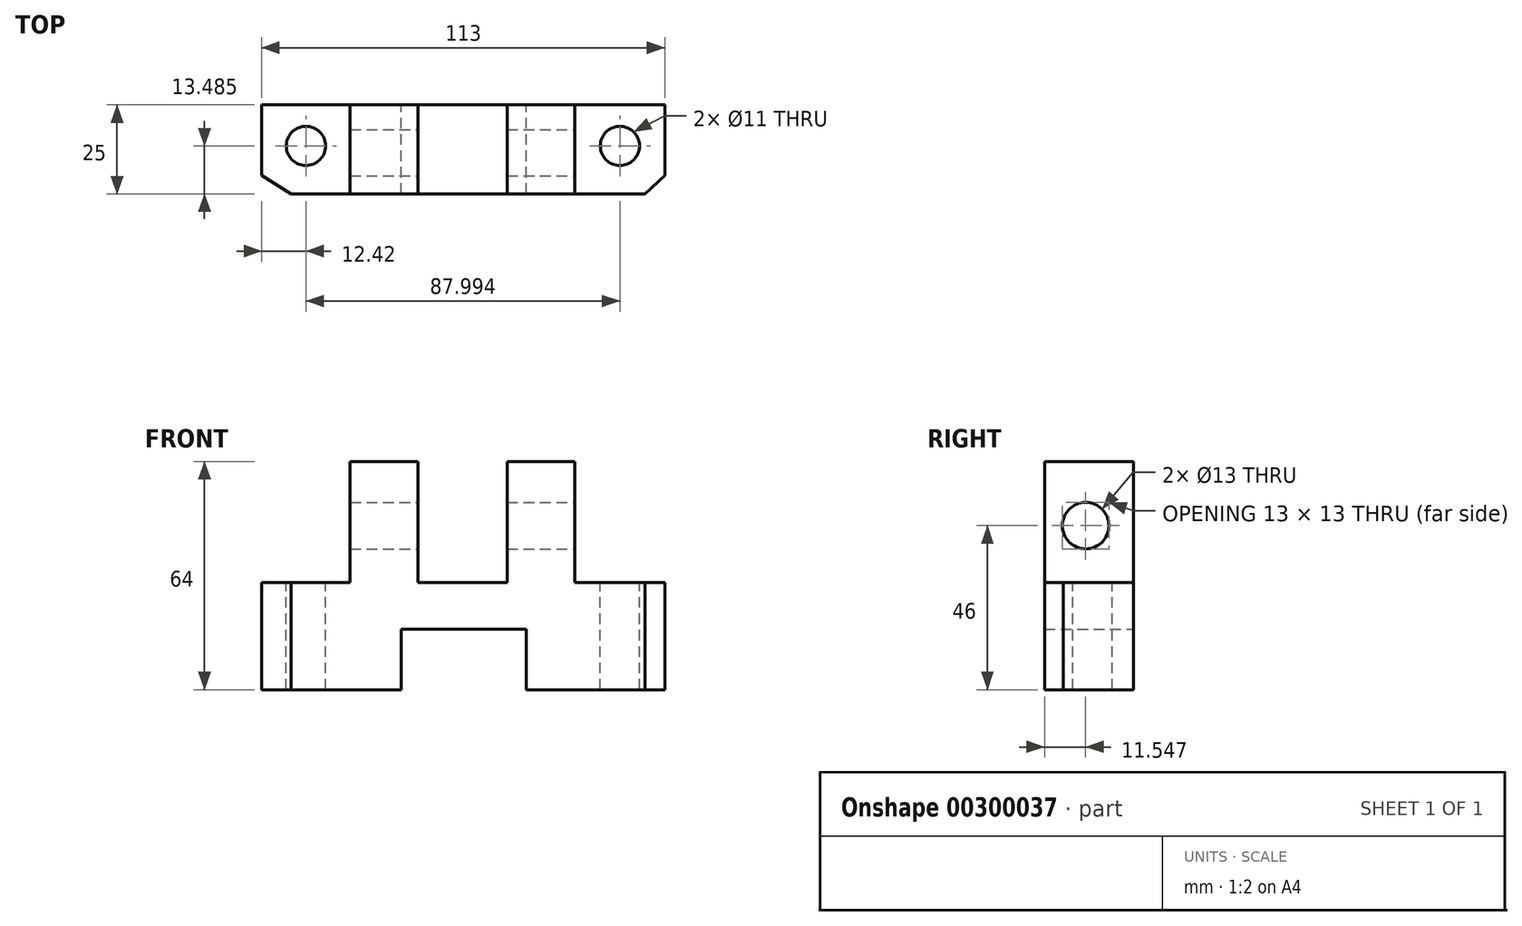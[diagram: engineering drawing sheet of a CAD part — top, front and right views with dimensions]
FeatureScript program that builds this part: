
annotation { "Feature Type Name" : "Feature", "Feature Type Description" : "" }
export const myFeature = defineFeature(function(context is Context, id is Id, definition is map)
    precondition{}
    {
        {
            var Q0;
            Q0=qCreatedBy(makeId("Front.planeOp"),FACE);
            var sketch = newSketch(context, id + "F0", { "sketchPlane" : qUnion([Q0])});
            skLineSegment(sketch, "E0", {"start": v(0, 0) * mm, "end": v(0, 30) * mm});
            skLineSegment(sketch, "E1", {"start": v(0, 30) * mm, "end": v(24.83, 30) * mm});
            skLineSegment(sketch, "E2", {"start": v(24.83, 30) * mm, "end": v(24.83, 64) * mm});
            skLineSegment(sketch, "E3", {"start": v(24.83, 64) * mm, "end": v(43.83, 64) * mm});
            skLineSegment(sketch, "E4", {"start": v(43.83, 64) * mm, "end": v(43.83, 30) * mm});
            skLineSegment(sketch, "E5", {"start": v(43.83, 30) * mm, "end": v(68.83, 30) * mm});
            skLineSegment(sketch, "E6", {"start": v(68.83, 30) * mm, "end": v(68.83, 64) * mm});
            skLineSegment(sketch, "E7", {"start": v(68.83, 64) * mm, "end": v(87.83, 64) * mm});
            skLineSegment(sketch, "E8", {"start": v(87.83, 64) * mm, "end": v(87.83, 30) * mm});
            skLineSegment(sketch, "E9", {"start": v(87.83, 30) * mm, "end": v(113, 30) * mm});
            skLineSegment(sketch, "E10", {"start": v(113, 30) * mm, "end": v(113, 0) * mm});
            skLineSegment(sketch, "E11", {"start": v(113, 0) * mm, "end": v(74.16, 0) * mm});
            skLineSegment(sketch, "E12", {"start": v(74.16, 0) * mm, "end": v(74.16, 17) * mm});
            skLineSegment(sketch, "E13", {"start": v(74.16, 17) * mm, "end": v(39.16, 17) * mm});
            skLineSegment(sketch, "E14", {"start": v(39.16, 17) * mm, "end": v(39.16, 0) * mm});
            skLineSegment(sketch, "E15", {"start": v(39.16, 0) * mm, "end": v(0, 0) * mm});
            skSolve(sketch);
        }
        {
            var Q0;
            Q0 = qSketchRegion(id + "F0", true);
            extrude(context, id + "F1", {"entities" : qUnion([Q0]), "depth" : 25 * mm});
        }
        {
            var Q0;
            Q0=makeQuery(id+"F1.opExtrude","SWEPT_FACE",FACE,{"disambiguationData":[OSD([sQuery(id+"F0.wireOp",EDGE,"E1")])]});
            var sketch = newSketch(context, id + "F2", { "sketchPlane" : qUnion([Q0])});
            skLineSegment(sketch, "E16", {"start": v(107.42, -25) * mm, "end": v(113, -19.74) * mm});
            skLineSegment(sketch, "E17", {"start": v(8.3, -25) * mm, "end": v(0, -19.74) * mm});
            skCircle(sketch, "E18", {"center": v(12.42, -11.51) * mm, "radius": 5.5 * mm});
            skCircle(sketch, "E19", {"center": v(100.41, -11.51) * mm, "radius": 5.5 * mm});
            skPoint(sketch, "E19.centerSnap0", {"position": v(100.41, -25) * mm});
            skLineSegment(sketch, "E20", {"start": v(0, -19.74) * mm, "end": v(0, -25) * mm});
            skLineSegment(sketch, "E21", {"start": v(0, -25) * mm, "end": v(8.3, -25) * mm});
            skLineSegment(sketch, "E22", {"start": v(113, -19.74) * mm, "end": v(113, -25) * mm});
            skLineSegment(sketch, "E23", {"start": v(113, -25) * mm, "end": v(107.42, -25) * mm});
            skSolve(sketch);
        }
        {
            var Q0;
            Q0=makeQuery(id+"F1.opExtrude","SWEPT_FACE",FACE,{"disambiguationData":[OSD([sQuery(id+"F0.wireOp",EDGE,"E8")])]});
            var sketch = newSketch(context, id + "F3", { "sketchPlane" : qUnion([Q0])});
            skCircle(sketch, "E24", {"center": v(-13.45, 46) * mm, "radius": 6.5 * mm});
            skSolve(sketch);
        }
        {
            var Q0;
            Q0 = qSketchRegion(id + "F3", true);
            extrude(context, id + "F4", {"entities" : qUnion([Q0]), "operationType" : NewBodyOperationType.REMOVE, "endBound" : BoundingType.THROUGH_ALL, "oppositeDirection" : true, "depth" : 25 * mm});
        }
        {
            var Q0;
            Q0=makeQuery(id+"F2.imprint","IMPRINT",FACE,{"disambiguationData":[TD([[makeQuery(id+"F2.imprint","IMPRINT",EDGE,{"derivedFrom":sQuery(id+"F2.wireOp",EDGE,"E17")}),1.0]])]});
            var Q1;
            Q1=makeQuery(id+"F2.imprint","IMPRINT",FACE,{"disambiguationData":[TD([[makeQuery(id+"F2.imprint","IMPRINT",EDGE,{"derivedFrom":sQuery(id+"F2.wireOp",EDGE,"E16")}),-1.0]])]});
            extrude(context, id + "F5", {"entities" : qUnion([Q0, Q1]), "operationType" : NewBodyOperationType.REMOVE, "endBound" : BoundingType.THROUGH_ALL, "oppositeDirection" : true, "depth" : 25 * mm});
        }
        {
            var Q0;
            Q0 = qSketchRegion(id + "F2", true);
            extrude(context, id + "F6", {"entities" : qUnion([Q0]), "operationType" : NewBodyOperationType.REMOVE, "endBound" : BoundingType.THROUGH_ALL, "oppositeDirection" : true, "depth" : 25 * mm});
        }
    });
